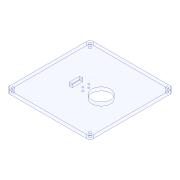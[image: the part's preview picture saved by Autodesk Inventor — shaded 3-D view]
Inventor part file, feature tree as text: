
AUTODESK INVENTOR PART (.ipt)
format: ipt  version: 2020 (Build 240168000, 168)  size: 133,120 bytes
history: native  units: mm
features: extrude x3, sketch x3, fillet x1
ambient origin geometry x8: Origin, YZ Plane, XZ Plane, XY Plane, X Axis, Y Axis, Z Axis, Center Point
bodies: Solid1 (feature_tree)
feature tree (7):
  extrude  "Extrusion1"  Depth=120.0mm
  extrude  "Extrusion2"  Depth=5.0mm
  fillet  "Fillet1"  Radius=110.0mm
  extrude  "Extrusion3"  Depth=4.0mm
  sketch  "Sketch1"  dims[d0=120.0mm d1=120.0mm]
  sketch  "Sketch2"  dims[d2=5.0mm d3=0.0mm d4=110.0mm d5=110.0mm]
  sketch  "Sketch4"  dims[d6=4.0mm d7=4.0mm d8=4.0mm d9=4.0mm d10=5.0mm d11=0.0mm d12=5.0mm d14=4.0mm d15=15.0mm d16=20.0mm d17=14.0mm d18=14.0mm d19=2.5mm d20=2.5mm d21=8.5mm d22=4.25mm d23=10.0mm d24=0.0mm d25=26.5mm d26=16.0mm]
